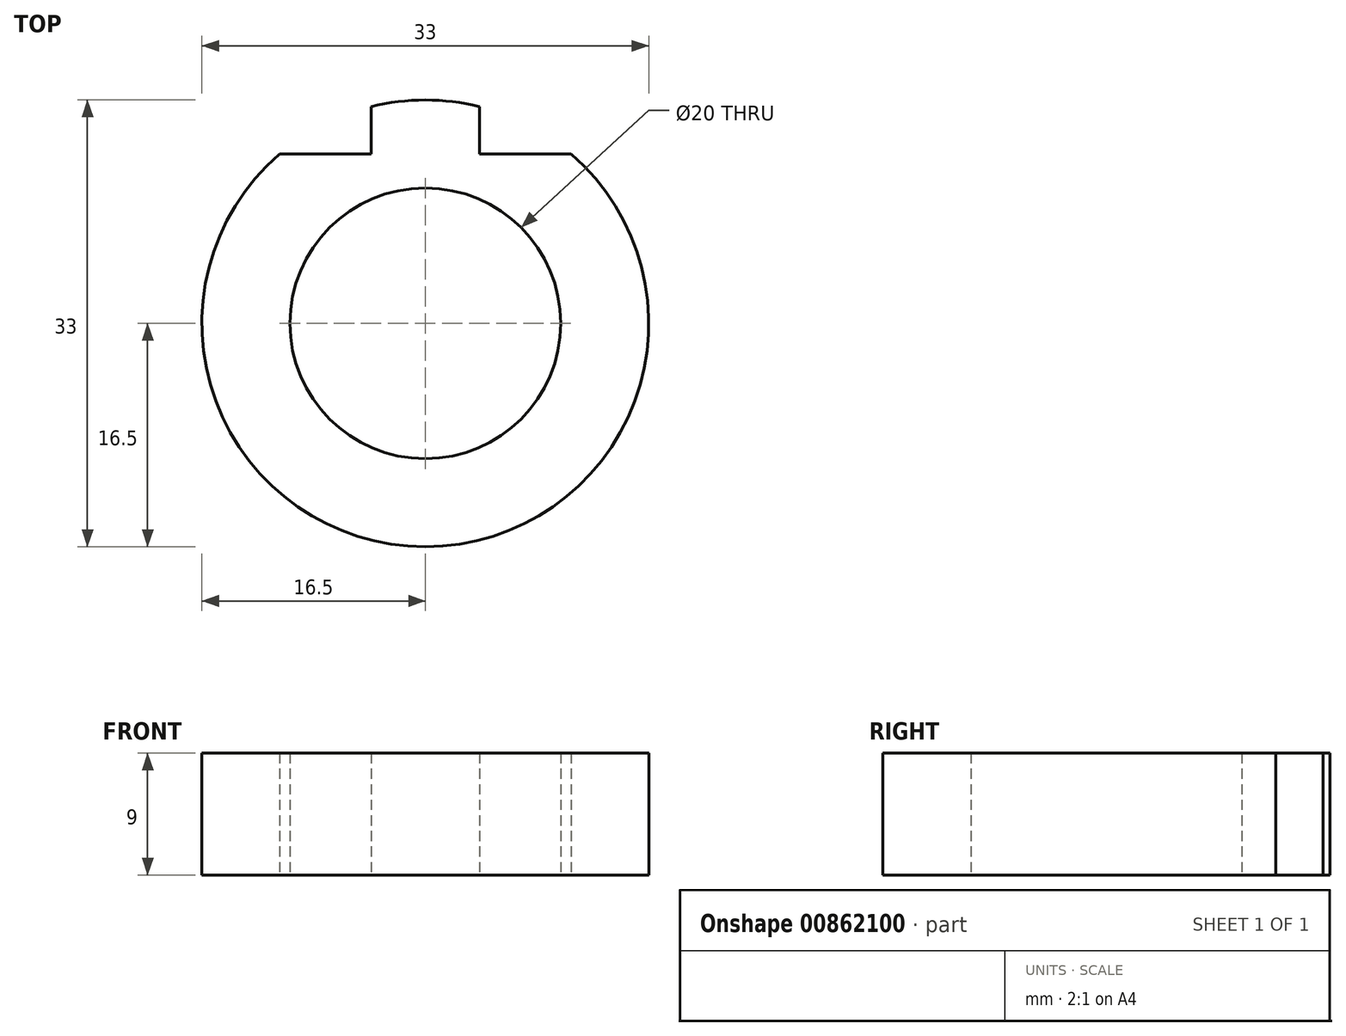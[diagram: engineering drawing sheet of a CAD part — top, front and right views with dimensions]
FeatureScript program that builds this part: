
annotation { "Feature Type Name" : "Feature", "Feature Type Description" : "" }
export const myFeature = defineFeature(function(context is Context, id is Id, definition is map)
    precondition{}
    {
        {
            var Q0;
            Q0=qCreatedBy(makeId("Top.planeOp"),FACE);
            var sketch = newSketch(context, id + "F0", { "sketchPlane" : qUnion([Q0])});
            skCircle(sketch, "E0", {"center": v(0, 0) * mm, "radius": 10 * mm});
            skCircle(sketch, "E1", {"center": v(0, 0) * mm, "radius": 16.5 * mm});
            skLineSegment(sketch, "E2", {"start": v(0, 16.5) * mm, "end": v(0, -16.5) * mm, "construction": true});
            skLineSegment(sketch, "E3", {"start": v(-4, 16) * mm, "end": v(-4, 12.5) * mm});
            skLineSegment(sketch, "E4", {"start": v(4, 16) * mm, "end": v(4, 12.5) * mm});
            skLineSegment(sketch, "E5", {"start": v(4, 12.5) * mm, "end": v(10.76, 12.5) * mm});
            skLineSegment(sketch, "E6", {"start": v(-4, 12.5) * mm, "end": v(-10.76, 12.5) * mm});
            skSolve(sketch);
        }
        {
            var Q0;
            Q0=makeQuery(id+"F0.imprint","IMPRINT",FACE,{"disambiguationData":[TD([[makeQuery(id+"F0.imprint","IMPRINT",EDGE,{"derivedFrom":sQuery(id+"F0.wireOp",EDGE,"E0")}),-1.0]])]});
            extrude(context, id + "F1", {"entities" : qUnion([Q0]), "depth" : 9 * mm, "offsetDistance" : 25 * mm});
        }
    });
